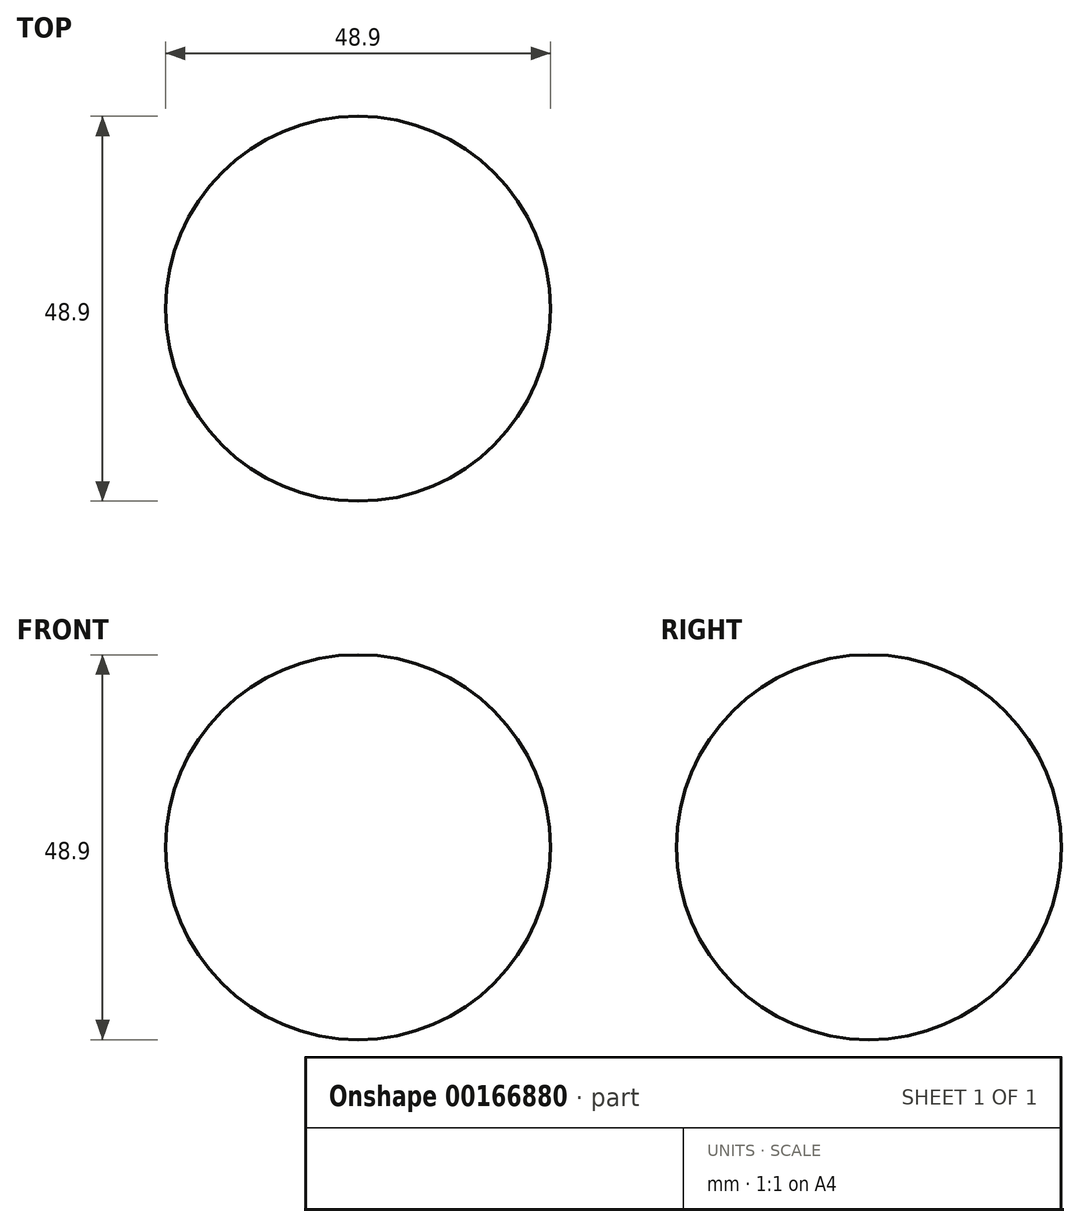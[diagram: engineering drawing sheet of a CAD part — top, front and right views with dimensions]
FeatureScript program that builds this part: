
annotation { "Feature Type Name" : "Feature", "Feature Type Description" : "" }
export const myFeature = defineFeature(function(context is Context, id is Id, definition is map)
    precondition{}
    {
        {
            var Q0;
            Q0=qCreatedBy(makeId("Top.planeOp"),FACE);
            var sketch = newSketch(context, id + "F0", { "sketchPlane" : qUnion([Q0])});
            skArc(sketch, "E0", {"start": v(0, 0) * mm, "mid": v(24.45, 24.45) * mm, "end": v(0, 48.9) * mm});
            skLineSegment(sketch, "E1", {"start": v(0, 48.9) * mm, "end": v(0, 0) * mm});
            skSolve(sketch);
        }
        {
            var Q0;
            Q0=makeQuery(id+"F0.imprint","IMPRINT",FACE,{"disambiguationData":[TD([[makeQuery(id+"F0.imprint","IMPRINT",EDGE,{"derivedFrom":sQuery(id+"F0.wireOp",EDGE,"E0")}),1.0]])]});
            var Q1;
            Q1=sQuery(id+"F0.wireOp",EDGE,"E1");
            revolve(context, id + "F1", {"entities" : qUnion([Q0]), "axis" : qUnion([Q1]), "revolveType" : RevolveType.FULL});
        }
    });
